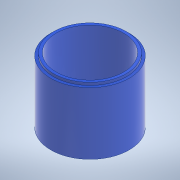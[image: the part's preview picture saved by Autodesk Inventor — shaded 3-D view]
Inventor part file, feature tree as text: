
AUTODESK INVENTOR PART (.ipt)
format: ipt  version: 2020 (Build 240168000, 168)  size: 130,560 bytes
history: native  units: mm
features: extrude x2, sketch x1
ambient origin geometry x8: Origin, YZ Plane, XZ Plane, XY Plane, X Axis, Y Axis, Z Axis, Center Point
bodies: Solid1 (feature_tree)
feature tree (3):
  sketch  "Sketch1"  dims[d0=50.0mm d1=54.0mm d2=58.0mm d3=46.0mm d4=0.0mm d5=44.0mm d6=2.0mm d7=0.0mm d8=0.0mm]
  extrude  "Extrusion1"  Depth=2.0mm
  extrude  "Extrusion2"  Depth=2.0mm
